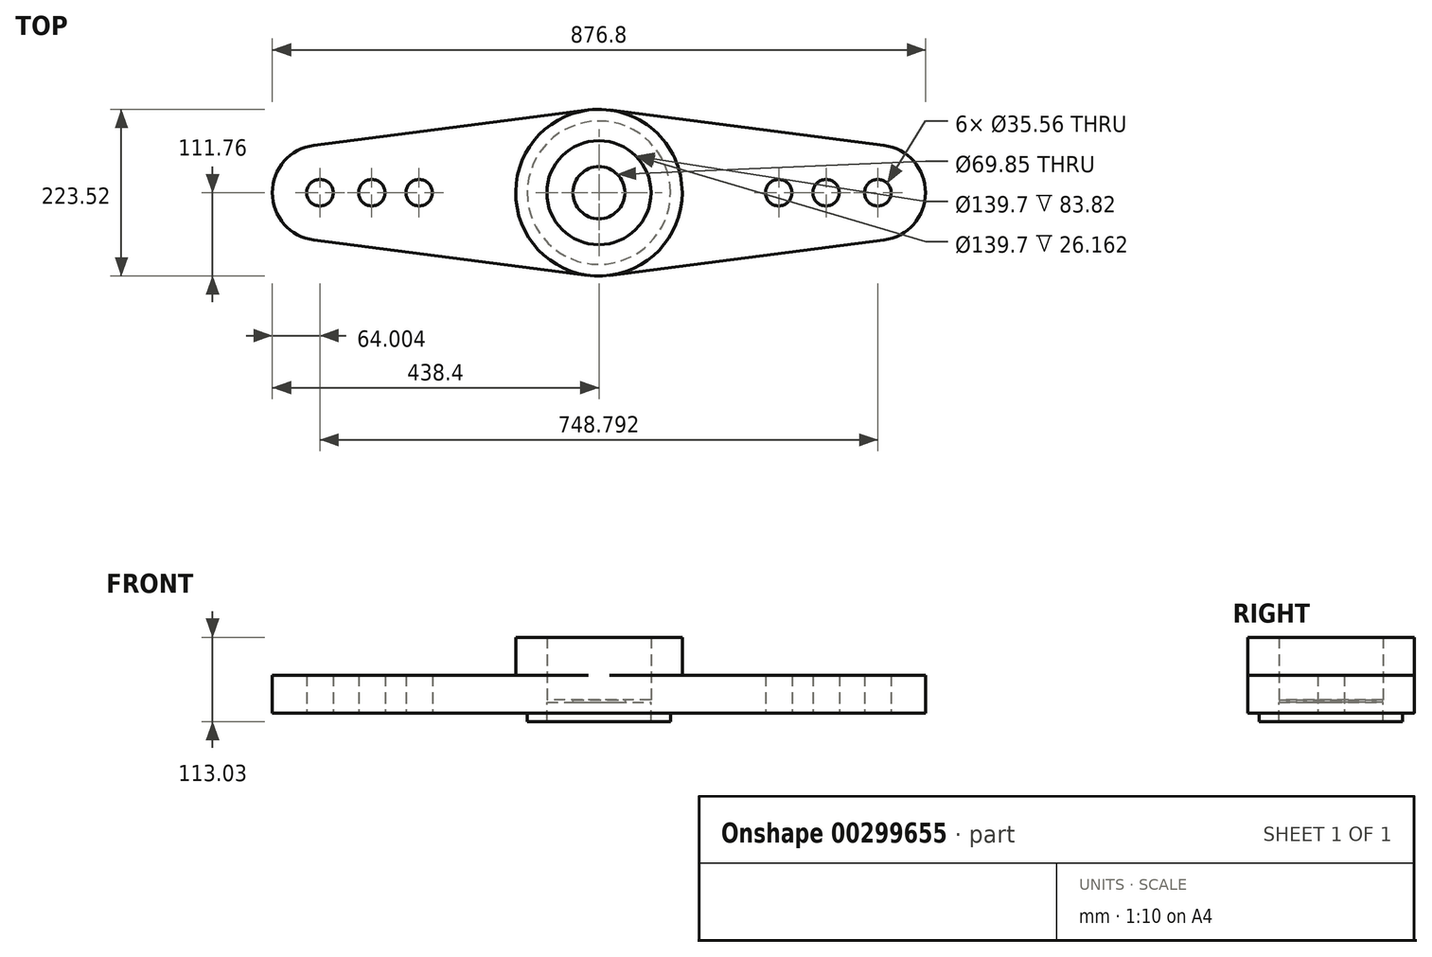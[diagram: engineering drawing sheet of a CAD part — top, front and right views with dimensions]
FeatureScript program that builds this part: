
annotation { "Feature Type Name" : "Feature", "Feature Type Description" : "" }
export const myFeature = defineFeature(function(context is Context, id is Id, definition is map)
    precondition{}
    {
        {
            var Q0;
            Q0=qCreatedBy(makeId("Top.planeOp"),FACE);
            var sketch = newSketch(context, id + "F0", { "sketchPlane" : qUnion([Q0])});
            skLineSegment(sketch, "E0", {"start": v(0, 0) * mm, "end": v(458.31, 0) * mm});
            skLineSegment(sketch, "E1", {"start": v(0, 0) * mm, "end": v(0, 223.4) * mm});
            skLineSegment(sketch, "E2", {"start": v(14.25, 110.85) * mm, "end": v(382.56, 63.49) * mm});
            skCircle(sketch, "E3", {"center": v(374.4, 0) * mm, "radius": 17.78 * mm});
            skCircle(sketch, "E4", {"center": v(304.8, 0) * mm, "radius": 17.78 * mm});
            skCircle(sketch, "E5", {"center": v(241.3, 0) * mm, "radius": 17.78 * mm});
            skCircle(sketch, "E6", {"center": v(0, 0) * mm, "radius": 34.93 * mm});
            skArc(sketch, "E7", {"start": v(382.56, 63.49) * mm, "mid": v(422.46, 42.28) * mm, "end": v(438.4, 0) * mm});
            skArc(sketch, "E8", {"start": v(0, 111.76) * mm, "mid": v(7.14, 111.53) * mm, "end": v(14.25, 110.85) * mm});
            skArc(sketch, "E9.MirrorCS", {"start": v(0, 111.76) * mm, "mid": v(-7.14, 111.53) * mm, "end": v(-14.25, 110.85) * mm});
            skLineSegment(sketch, "E10.MirrorCS", {"start": v(-14.25, 110.85) * mm, "end": v(-382.56, 63.49) * mm});
            skArc(sketch, "E11.MirrorCS", {"start": v(-382.56, 63.49) * mm, "mid": v(-422.46, 42.28) * mm, "end": v(-438.4, 0) * mm});
            skCircle(sketch, "E12.MirrorC", {"center": v(-374.4, 0) * mm, "radius": 17.78 * mm});
            skCircle(sketch, "E13.MirrorC", {"center": v(-304.8, 0) * mm, "radius": 17.78 * mm});
            skCircle(sketch, "E14.MirrorC", {"center": v(-241.3, 0) * mm, "radius": 17.78 * mm});
            skArc(sketch, "E15.MirrorCS", {"start": v(-382.56, -63.49) * mm, "mid": v(-422.46, -42.28) * mm, "end": v(-438.4, 0) * mm});
            skLineSegment(sketch, "E16.MirrorCS", {"start": v(-14.25, -110.85) * mm, "end": v(-382.56, -63.49) * mm});
            skArc(sketch, "E17.MirrorCS", {"start": v(0, -111.76) * mm, "mid": v(-7.14, -111.53) * mm, "end": v(-14.25, -110.85) * mm});
            skArc(sketch, "E18.MirrorCS", {"start": v(0, -111.76) * mm, "mid": v(7.14, -111.53) * mm, "end": v(14.25, -110.85) * mm});
            skLineSegment(sketch, "E19.MirrorCS", {"start": v(14.25, -110.85) * mm, "end": v(382.56, -63.49) * mm});
            skArc(sketch, "E20.MirrorCS", {"start": v(382.56, -63.49) * mm, "mid": v(422.46, -42.28) * mm, "end": v(438.4, 0) * mm});
            skSolve(sketch);
        }
        {
            var Q0;
            {var subQ0=sQuery(id+"F0.wireOp",EDGE,"E9.MirrorCS");Q0=makeQuery(id+"F0.imprint","IMPRINT",FACE,{"disambiguationData":[TD([[makeQuery(id+"F0.imprint","IMPRINT",EDGE,{"derivedFrom":subQ0}),1.0]])]});}
            var Q1;
            Q1=makeQuery(id+"F0.imprint","IMPRINT",FACE,{"disambiguationData":[TD([[makeQuery(id+"F0.imprint","IMPRINT",EDGE,{"derivedFrom":sQuery(id+"F0.wireOp",EDGE,"E2")}),-1.0]])]});
            extrude(context, id + "F1", {"entities" : qUnion([Q0, Q1]), "depth" : 50.8 * mm});
        }
        {
            var Q0;
            Q0=makeQuery(id+"F1.opExtrude","CAP_FACE",FACE,{"disambiguationData":[OSD([sQuery(id+"F0.wireOp",EDGE,"E2"),sQuery(id+"F0.wireOp",EDGE,"E3"),sQuery(id+"F0.wireOp",EDGE,"E4"),sQuery(id+"F0.wireOp",EDGE,"E5"),sQuery(id+"F0.wireOp",EDGE,"E6"),sQuery(id+"F0.wireOp",EDGE,"E7"),sQuery(id+"F0.wireOp",EDGE,"E8"),sQuery(id+"F0.wireOp",EDGE,"E9.MirrorCS"),sQuery(id+"F0.wireOp",EDGE,"E10.MirrorCS"),sQuery(id+"F0.wireOp",EDGE,"E11.MirrorCS"),sQuery(id+"F0.wireOp",EDGE,"E12.MirrorC"),sQuery(id+"F0.wireOp",EDGE,"E13.MirrorC"),sQuery(id+"F0.wireOp",EDGE,"E14.MirrorC"),sQuery(id+"F0.wireOp",EDGE,"E15.MirrorCS"),sQuery(id+"F0.wireOp",EDGE,"E16.MirrorCS"),sQuery(id+"F0.wireOp",EDGE,"E17.MirrorCS"),sQuery(id+"F0.wireOp",EDGE,"E18.MirrorCS"),sQuery(id+"F0.wireOp",EDGE,"E19.MirrorCS"),sQuery(id+"F0.wireOp",EDGE,"E20.MirrorCS")])],"isStart":false});
            var sketch = newSketch(context, id + "F2", { "sketchPlane" : qUnion([Q0])});
            skCircle(sketch, "E21", {"center": v(0, 0) * mm, "radius": 111.76 * mm});
            skCircle(sketch, "E22", {"center": v(0, 0) * mm, "radius": 69.85 * mm});
            skSolve(sketch);
        }
        {
            var Q0;
            Q0 = qSketchRegion(id + "F2", true);
            extrude(context, id + "F3", {"entities" : qUnion([Q0]), "operationType" : NewBodyOperationType.ADD, "depth" : 50.8 * mm});
        }
        {
            var Q0;
            Q0=makeQuery(id+"F3.opExtrude","CAP_FACE",FACE,{"disambiguationData":[OSD([sQuery(id+"F2.wireOp",EDGE,"E21"),sQuery(id+"F2.wireOp",EDGE,"E22")])],"isStart":false});
            var sketch = newSketch(context, id + "F4", { "sketchPlane" : qUnion([Q0])});
            skCircle(sketch, "E23", {"center": v(0, 0) * mm, "radius": 69.85 * mm});
            skSolve(sketch);
        }
        {
            var Q0;
            Q0 = qSketchRegion(id + "F4", true);
            extrude(context, id + "F5", {"entities" : qUnion([Q0]), "operationType" : NewBodyOperationType.REMOVE, "oppositeDirection" : true, "depth" : 83.82 * mm});
        }
        {
            var Q0;
            Q0=makeQuery(id+"F1.opExtrude","CAP_FACE",FACE,{"disambiguationData":[OSD([sQuery(id+"F0.wireOp",EDGE,"E2"),sQuery(id+"F0.wireOp",EDGE,"E3"),sQuery(id+"F0.wireOp",EDGE,"E4"),sQuery(id+"F0.wireOp",EDGE,"E5"),sQuery(id+"F0.wireOp",EDGE,"E6"),sQuery(id+"F0.wireOp",EDGE,"E7"),sQuery(id+"F0.wireOp",EDGE,"E8"),sQuery(id+"F0.wireOp",EDGE,"E9.MirrorCS"),sQuery(id+"F0.wireOp",EDGE,"E10.MirrorCS"),sQuery(id+"F0.wireOp",EDGE,"E11.MirrorCS"),sQuery(id+"F0.wireOp",EDGE,"E12.MirrorC"),sQuery(id+"F0.wireOp",EDGE,"E13.MirrorC"),sQuery(id+"F0.wireOp",EDGE,"E14.MirrorC"),sQuery(id+"F0.wireOp",EDGE,"E15.MirrorCS"),sQuery(id+"F0.wireOp",EDGE,"E16.MirrorCS"),sQuery(id+"F0.wireOp",EDGE,"E17.MirrorCS"),sQuery(id+"F0.wireOp",EDGE,"E18.MirrorCS"),sQuery(id+"F0.wireOp",EDGE,"E19.MirrorCS"),sQuery(id+"F0.wireOp",EDGE,"E20.MirrorCS")])],"isStart":true});
            var sketch = newSketch(context, id + "F6", { "sketchPlane" : qUnion([Q0])});
            skCircle(sketch, "E24", {"center": v(0, 0) * mm, "radius": 96.14 * mm});
            skCircle(sketch, "E25", {"center": v(0, 0) * mm, "radius": 69.85 * mm});
            skSolve(sketch);
        }
        {
            var Q0;
            Q0 = qSketchRegion(id + "F6", true);
            extrude(context, id + "F7", {"entities" : qUnion([Q0]), "operationType" : NewBodyOperationType.ADD, "depth" : 11.43 * mm});
        }
        {
            var Q0;
            Q0=makeQuery(id+"F7.opExtrude","CAP_FACE",FACE,{"disambiguationData":[OSD([sQuery(id+"F6.wireOp",EDGE,"E24"),sQuery(id+"F6.wireOp",EDGE,"E25")])],"isStart":false});
            var sketch = newSketch(context, id + "F8", { "sketchPlane" : qUnion([Q0])});
            skCircle(sketch, "E26", {"center": v(0, 0) * mm, "radius": 69.85 * mm});
            skSolve(sketch);
        }
        {
            var Q0;
            Q0 = qSketchRegion(id + "F8", true);
            extrude(context, id + "F9", {"entities" : qUnion([Q0]), "operationType" : NewBodyOperationType.REMOVE, "oppositeDirection" : true, "depth" : 26.16 * mm});
        }
    });
